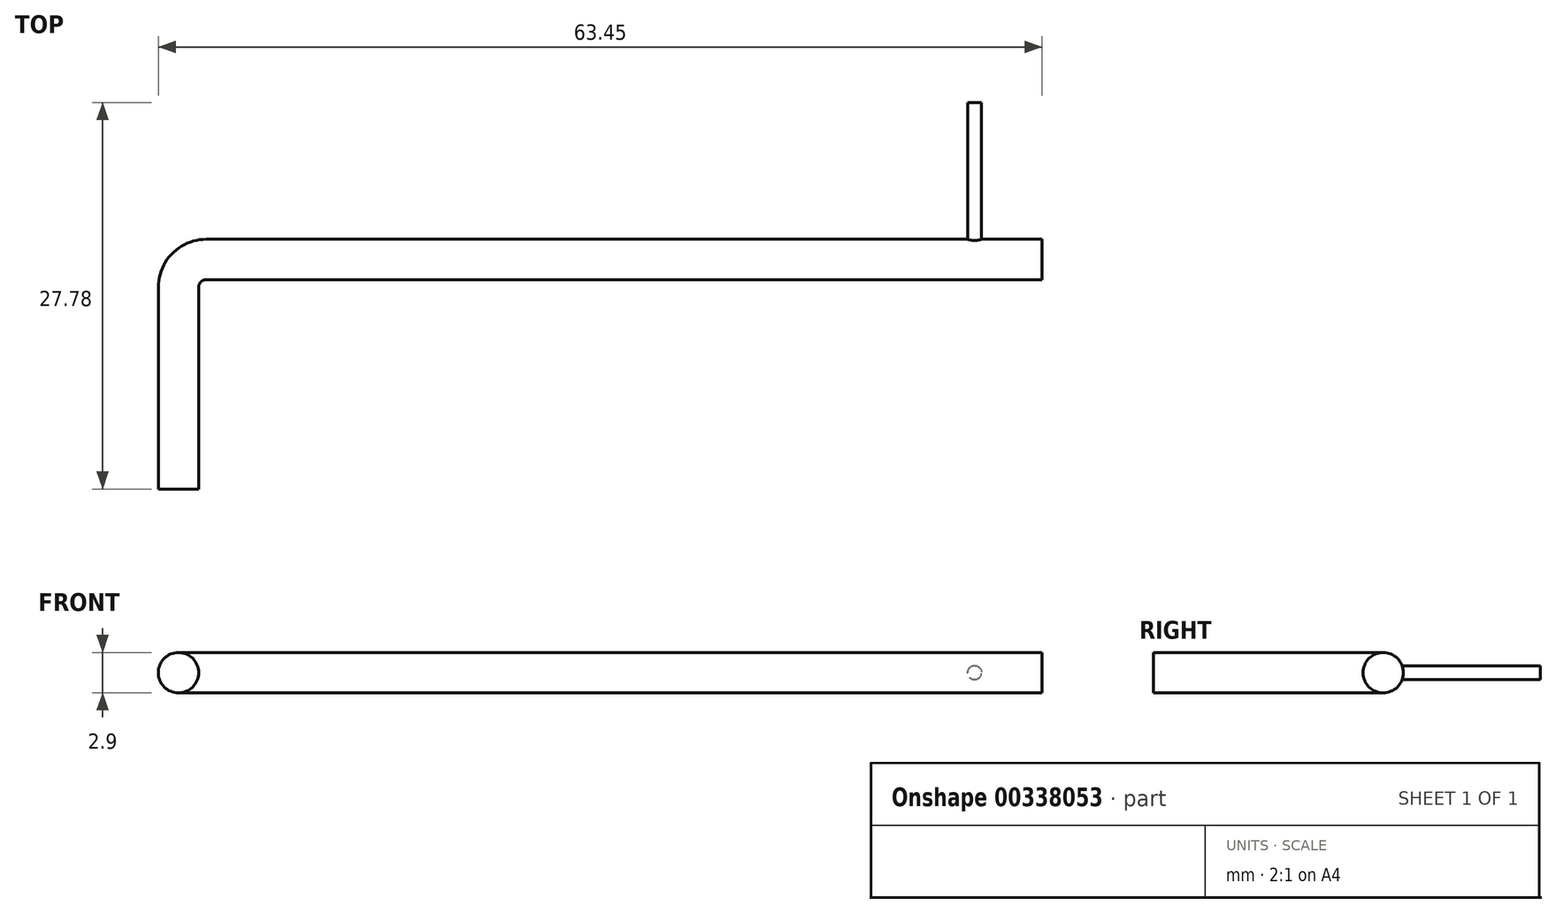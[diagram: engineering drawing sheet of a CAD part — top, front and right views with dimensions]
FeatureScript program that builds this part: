
annotation { "Feature Type Name" : "Feature", "Feature Type Description" : "" }
export const myFeature = defineFeature(function(context is Context, id is Id, definition is map)
    precondition{}
    {
        {
            var Q0;
            Q0=qCreatedBy(makeId("Front.planeOp"),FACE);
            cPlane(context, id + "F0", {"entities" : qUnion([Q0]), "cplaneType" : CPlaneType.OFFSET, "offset" : 16.5 * mm, "width" : 150 * mm, "height" : 150 * mm});
        }
        {
            var Q0;
            Q0=qCreatedBy(makeId("Top.planeOp"),FACE);
            var sketch = newSketch(context, id + "F1", { "sketchPlane" : qUnion([Q0])});
            skLineSegment(sketch, "E0", {"start": v(-73.95, 0) * mm, "end": v(-13.95, 0) * mm});
            skLineSegment(sketch, "E1", {"start": v(-75.95, -2) * mm, "end": v(-75.95, -16.5) * mm});
            skPoint(sketch, "E2.visualSharp", {"position": v(-75.95, 0) * mm});
            skArc(sketch, "E2.filletArc", {"start": v(-73.95, 0) * mm, "mid": v(-75.36, -0.59) * mm, "end": v(-75.95, -2) * mm});
            skSolve(sketch);
        }
        {
            var Q0;
            Q0=qCreatedBy(id+"F0.planeOp",FACE);
            var sketch = newSketch(context, id + "F2", { "sketchPlane" : qUnion([Q0])});
            skLineSegment(sketch, "E3", {"start": v(0, 22.68) * mm, "end": v(0, -22.65) * mm, "construction": true});
            skCircle(sketch, "E4", {"center": v(-75.95, 0) * mm, "radius": 1.45 * mm});
            skSolve(sketch);
        }
        {
            var Q0;
            Q0=makeQuery(id+"F2.imprint","IMPRINT",FACE,{"disambiguationData":[TD([[makeQuery(id+"F2.imprint","IMPRINT",EDGE,{"derivedFrom":sQuery(id+"F2.wireOp",EDGE,"E4")}),1.0]])]});
            var Q1;
            Q1=qConstructionFilter(qBodyType(qCreatedBy(id+"F1",EDGE),BodyType.WIRE),ConstructionObject.NO);
            sweep(context, id + "F3", {"profiles" : qUnion([Q0]), "path" : qUnion([Q1])});
        }
        {
            var Q0;
            Q0=qCreatedBy(makeId("Front.planeOp"),FACE);
            cPlane(context, id + "F4", {"entities" : qUnion([Q0]), "cplaneType" : CPlaneType.OFFSET, "offset" : (13 - 1.72) * mm, "oppositeDirection" : true, "width" : 150 * mm, "height" : 150 * mm});
        }
        {
            var Q0;
            Q0=qCreatedBy(id+"F4.planeOp",FACE);
            var sketch = newSketch(context, id + "F5", { "sketchPlane" : qUnion([Q0])});
            skPoint(sketch, "E5", {"position": v(-18.8, 0) * mm});
            skPoint(sketch, "E6", {"position": v(-75.95, 0) * mm});
            skCircle(sketch, "E7", {"center": v(-18.8, 0) * mm, "radius": 0.5 * mm});
            skSolve(sketch);
        }
        {
            var Q0;
            Q0=qSketchRegion(id+"F5",true);
            var Q1;
            Q1=makeQuery(id+"F3.opSweep","SWEPT_BODY",BODY,{"disambiguationData":[OSD([sQuery(id+"F1.wireOp",EDGE,"E1"),sQuery(id+"F2.wireOp",EDGE,"E4")])]});
            extrude(context, id + "F6", {"entities" : qUnion([Q0]), "operationType" : NewBodyOperationType.ADD, "endBound" : BoundingType.UP_TO_BODY, "endBoundEntityBody" : qUnion([Q1]), "depth" : 25 * mm});
        }
    });
